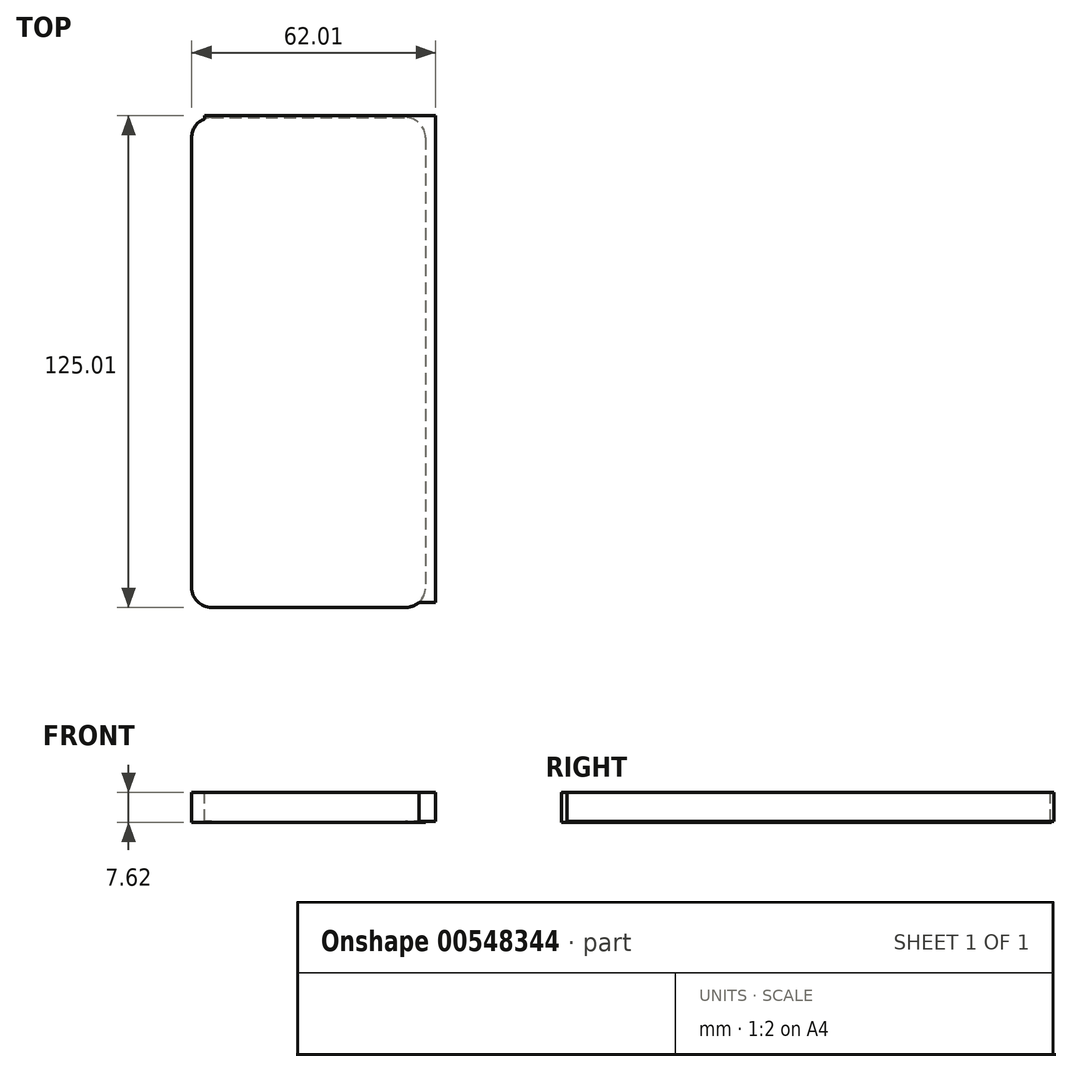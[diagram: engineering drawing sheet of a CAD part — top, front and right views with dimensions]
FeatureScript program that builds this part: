
annotation { "Feature Type Name" : "Feature", "Feature Type Description" : "" }
export const myFeature = defineFeature(function(context is Context, id is Id, definition is map)
    precondition{}
    {
        {
            var Q0;
            Q0=qCreatedBy(makeId("Top.planeOp"),FACE);
            var sketch = newSketch(context, id + "F0", { "sketchPlane" : qUnion([Q0])});
            skLineSegment(sketch, "E0.bottom", {"start": v(-28.06, 69.22) * mm, "end": v(31.38, 69.22) * mm});
            skLineSegment(sketch, "E0.top", {"start": v(-28.06, -55.24) * mm, "end": v(31.38, -55.24) * mm});
            skLineSegment(sketch, "E0.left", {"start": v(-28.06, 69.22) * mm, "end": v(-28.06, -55.24) * mm});
            skLineSegment(sketch, "E0.right", {"start": v(31.38, 69.22) * mm, "end": v(31.38, -55.24) * mm});
            skSolve(sketch);
        }
        {
            var Q0;
            Q0=makeQuery(id+"F0.imprint","IMPRINT",FACE,{"disambiguationData":[TD([[makeQuery(id+"F0.imprint","IMPRINT",EDGE,{"derivedFrom":sQuery(id+"F0.wireOp",EDGE,"E0.bottom")}),-1.0]])]});
            extrude(context, id + "F1", {"entities" : qUnion([Q0]), "depth" : 7.62 * mm, "offsetDistance" : 25.4 * mm});
        }
        {
            var Q0;
            Q0=makeQuery(id+"F1.opExtrude","SWEPT_EDGE",EDGE,{"disambiguationData":[OSD([sQuery(id+"F0.wireOp",EDGE,"E0.top"),sQuery(id+"F0.wireOp",EDGE,"E0.right")])]});
            var Q1;
            Q1=makeQuery(id+"F1.opExtrude","SWEPT_EDGE",EDGE,{"disambiguationData":[OSD([sQuery(id+"F0.wireOp",EDGE,"E0.top"),sQuery(id+"F0.wireOp",EDGE,"E0.left")])]});
            var Q2;
            Q2=makeQuery(id+"F1.opExtrude","SWEPT_EDGE",EDGE,{"disambiguationData":[OSD([sQuery(id+"F0.wireOp",EDGE,"E0.bottom"),sQuery(id+"F0.wireOp",EDGE,"E0.right")])]});
            var Q3;
            Q3=makeQuery(id+"F1.opExtrude","SWEPT_EDGE",EDGE,{"disambiguationData":[OSD([sQuery(id+"F0.wireOp",EDGE,"E0.bottom"),sQuery(id+"F0.wireOp",EDGE,"E0.left")])]});
            fillet(context, id + "F2", {"entities" : qUnion([Q0, Q1, Q2, Q3]), "radius" : 5.08 * mm, "tangentPropagation" : true, "allowEdgeOverflow" : false});
        }
        {
            var Q0;
            Q0=makeQuery(id+"F1.opExtrude","CAP_FACE",FACE,{"disambiguationData":[OSD([sQuery(id+"F0.wireOp",EDGE,"E0.bottom"),sQuery(id+"F0.wireOp",EDGE,"E0.top"),sQuery(id+"F0.wireOp",EDGE,"E0.left"),sQuery(id+"F0.wireOp",EDGE,"E0.right")])],"isStart":false});
            var sketch = newSketch(context, id + "F3", { "sketchPlane" : qUnion([Q0])});
            skPoint(sketch, "E1.oppositeSnap0", {"position": v(33.95, -53.75) * mm});
            skLineSegment(sketch, "E1.bottom", {"start": v(-24.72, 69.77) * mm, "end": v(33.95, 69.77) * mm});
            skLineSegment(sketch, "E1.top", {"start": v(-24.72, -53.93) * mm, "end": v(33.95, -53.93) * mm});
            skLineSegment(sketch, "E1.left", {"start": v(-24.72, 69.77) * mm, "end": v(-24.72, -53.93) * mm});
            skLineSegment(sketch, "E1.right", {"start": v(33.95, 69.77) * mm, "end": v(33.95, -53.93) * mm});
            skPoint(sketch, "E2", {"position": v(-26.57, 69.77) * mm});
            skSolve(sketch);
        }
        {
            var Q0;
            {var subQ1=sQuery(id+"F3.wireOp",EDGE,"E1.bottom");Q0=makeQuery(id+"F3.imprint","IMPRINT",FACE,{"disambiguationData":[TD([[makeQuery(id+"F3.imprint","IMPRINT",EDGE,{"derivedFrom":subQ1}),-1.0]])]});}
            extrude(context, id + "F4", {"entities" : qUnion([Q0]), "operationType" : NewBodyOperationType.ADD, "oppositeDirection" : true, "depth" : 7.37 * mm, "offsetDistance" : 25.4 * mm});
        }
    });
